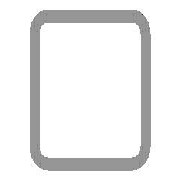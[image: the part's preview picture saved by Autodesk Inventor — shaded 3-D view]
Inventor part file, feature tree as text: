
AUTODESK INVENTOR PART (.ipt)
format: ipt  version: 2025 (Build 290162010, 162A)  size: 128,000 bytes
history: native  units: mm (DEFAULTED — no unit token found)
features: other x3, sketch x1, plane x1
ambient origin geometry x8: Origin, YZ Plane, XZ Plane, XY Plane, X Axis, Y Axis, Z Axis, Center Point
bodies: Solid1 (feature_tree), Body (feature_tree)
feature tree (5):
  other  "Driven Length"
  other  "Start plane"
  other  "End plane"
  sketch  "Sketch3"  dims[d3=2797.0mm d4=0.0mm d7=4.0mm d9=50.0mm d11=50.0mm d12=2.0mm d13=-0.0mm d14=2797.0mm d15=25.0mm d16=25.0mm d17=90.0deg d18=2797.0mm]
  plane  "Work Plane3"
